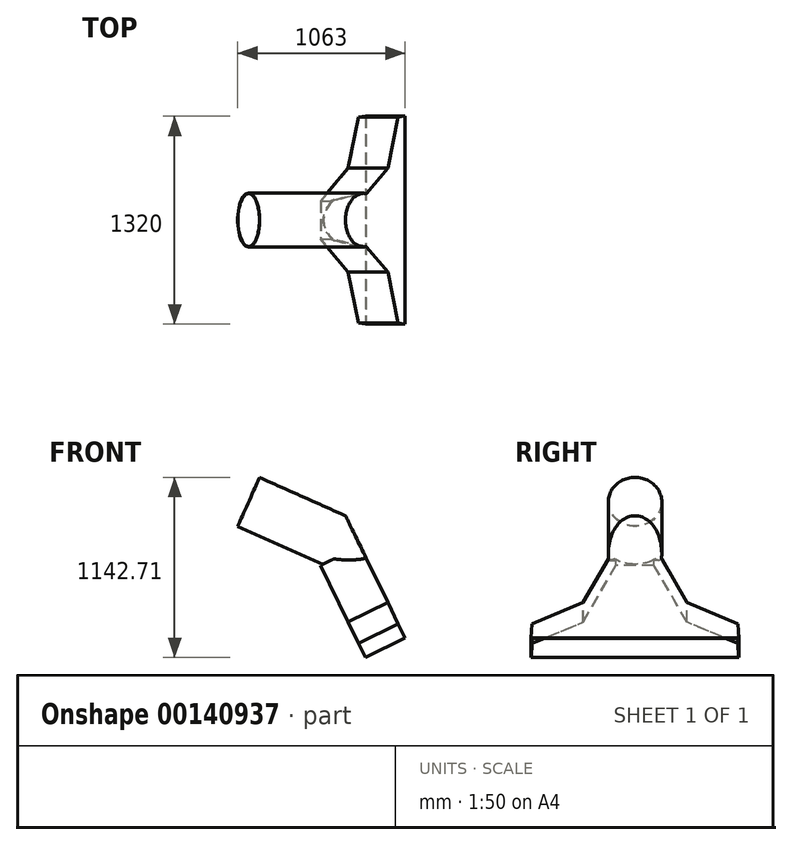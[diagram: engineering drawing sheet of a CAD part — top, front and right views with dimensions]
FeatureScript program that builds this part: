
annotation { "Feature Type Name" : "Feature", "Feature Type Description" : "" }
export const myFeature = defineFeature(function(context is Context, id is Id, definition is map)
    precondition{}
    {
        {
            var Q0;
            Q0=qCreatedBy(makeId("Front.planeOp"),FACE);
            var sketch = newSketch(context, id + "F0", { "sketchPlane" : qUnion([Q0])});
            skLineSegment(sketch, "E0", {"start": v(0, 0) * mm, "end": v(-33.98, 69.66) * mm});
            skSolve(sketch);
        }
        {
            var Q0;
            Q0=qCreatedBy(makeId("Right.planeOp"),FACE);
            var sketch = newSketch(context, id + "F1", { "sketchPlane" : qUnion([Q0])});
            skLineSegment(sketch, "E1", {"start": v(0, 0) * mm, "end": v(61.93, 0) * mm});
            skSolve(sketch);
        }
        {
            var Q0;
            Q0=sQuery(id+"F1.wireOp",EDGE,"E1");
            var Q1;
            Q1=sQuery(id+"F0.wireOp",EDGE,"E0");
            cPlane(context, id + "F2", {"entities" : qUnion([Q0, Q1]), "cplaneType" : CPlaneType.LINE_ANGLE, "offset" : 25 * mm, "angle" : 0 * degree, "width" : 150 * mm, "height" : 150 * mm});
        }
        {
            var Q0;
            Q0=qCreatedBy(id+"F2.planeOp",FACE);
            var sketch = newSketch(context, id + "F3", { "sketchPlane" : qUnion([Q0])});
            skLineSegment(sketch, "E2", {"start": v(0, 0) * mm, "end": v(-660, 0) * mm});
            skLineSegment(sketch, "E3", {"start": v(-660, 0) * mm, "end": v(-654.76, 100) * mm});
            skLineSegment(sketch, "E4", {"start": v(-654.76, 100) * mm, "end": v(-330, 250) * mm});
            skLineSegment(sketch, "E5", {"start": v(-330, 250) * mm, "end": v(-121.77, 650) * mm});
            skLineSegment(sketch, "E6", {"start": v(-121.77, 650) * mm, "end": v(0, 650) * mm});
            skLineSegment(sketch, "E7", {"start": v(0, 0) * mm, "end": v(0, 789.5) * mm, "construction": true});
            skLineSegment(sketch, "E8.MirrorCS", {"start": v(121.77, 650) * mm, "end": v(0, 650) * mm});
            skLineSegment(sketch, "E9.MirrorCS", {"start": v(330, 250) * mm, "end": v(121.77, 650) * mm});
            skLineSegment(sketch, "E10.MirrorCS", {"start": v(654.76, 100) * mm, "end": v(330, 250) * mm});
            skLineSegment(sketch, "E11.MirrorCS", {"start": v(660, 0) * mm, "end": v(654.76, 100) * mm});
            skLineSegment(sketch, "E12.MirrorCS", {"start": v(0, 0) * mm, "end": v(660, 0) * mm});
            skLineSegment(sketch, "E13", {"start": v(-660, 0) * mm, "end": v(-660, 232.34) * mm, "construction": true});
            skPoint(sketch, "E14", {"position": v(0, 600) * mm});
            skSolve(sketch);
        }
        {
            var Q0;
            Q0=makeQuery(id+"F3.imprint","IMPRINT",FACE,{"disambiguationData":[TD([[makeQuery(id+"F3.imprint","IMPRINT",EDGE,{"derivedFrom":sQuery(id+"F3.wireOp",EDGE,"E2")}),-1.0]])]});
            var Q1;
            Q1=qCreatedBy(makeId("Right.planeOp"),FACE);
            extrude(context, id + "F4", {"entities" : qUnion([Q0]), "oppositeDirection" : true, "endBoundEntityFace" : qUnion([Q1]), "depth" : 280 * mm});
        }
        {
            var Q0;
            Q0=qCreatedBy(makeId("Front.planeOp"),FACE);
            var sketch = newSketch(context, id + "F5", { "sketchPlane" : qUnion([Q0])});
            skLineSegment(sketch, "E15", {"start": v(-263.02, 539.28) * mm, "end": v(-993.86, 864.67) * mm});
            skSolve(sketch);
        }
        {
            var Q0;
            Q0=sQuery(id+"F5.wireOp",VERTEX,"E15.end");
            var Q1;
            Q1=sQuery(id+"F5.wireOp",EDGE,"E15");
            cPlane(context, id + "F6", {"entities" : qUnion([Q0, Q1]), "cplaneType" : CPlaneType.LINE_POINT, "offset" : 25 * mm, "width" : 150 * mm, "height" : 150 * mm});
        }
        {
            var Q0;
            Q0=qCreatedBy(id+"F6.planeOp",FACE);
            var sketch = newSketch(context, id + "F7", { "sketchPlane" : qUnion([Q0])});
            skCircle(sketch, "E16", {"center": v(0, 385.67) * mm, "radius": 170 * mm});
            skSolve(sketch);
        }
        {
            var Q0;
            Q0=makeQuery(id+"F7.imprint","IMPRINT",FACE,{"disambiguationData":[TD([[makeQuery(id+"F7.imprint","IMPRINT",EDGE,{"derivedFrom":sQuery(id+"F7.wireOp",EDGE,"E16")}),1.0]])]});
            var Q1;
            Q1=makeQuery(id+"F4.opExtrude","CAP_FACE",FACE,{"disambiguationData":[OSD([sQuery(id+"F3.wireOp",EDGE,"E2"),sQuery(id+"F3.wireOp",EDGE,"E3"),sQuery(id+"F3.wireOp",EDGE,"E4"),sQuery(id+"F3.wireOp",EDGE,"E5"),sQuery(id+"F3.wireOp",EDGE,"E6"),sQuery(id+"F3.wireOp",EDGE,"E8.MirrorCS"),sQuery(id+"F3.wireOp",EDGE,"E9.MirrorCS"),sQuery(id+"F3.wireOp",EDGE,"E10.MirrorCS"),sQuery(id+"F3.wireOp",EDGE,"E11.MirrorCS"),sQuery(id+"F3.wireOp",EDGE,"E12.MirrorCS")])],"isStart":true});
            extrude(context, id + "F8", {"entities" : qUnion([Q0]), "operationType" : NewBodyOperationType.ADD, "endBound" : BoundingType.UP_TO_SURFACE, "oppositeDirection" : true, "endBoundEntityFace" : qUnion([Q1]), "depth" : 25 * mm});
        }
        {
            var Q0;
            Q0=makeQuery(id+"F8.opExtrude","CAP_FACE",FACE,{"disambiguationData":[OSD([sQuery(id+"F7.wireOp",EDGE,"E16")])],"isStart":true});
            var Q1;
            Q1=makeQuery(id+"F4.opExtrude","SWEPT_FACE",FACE,{"disambiguationData":[OSD([sQuery(id+"F3.wireOp",EDGE,"E2"),sQuery(id+"F3.wireOp",EDGE,"E12.MirrorCS")])]});
            shell(context, id + "F9", {"entities" : qUnion([Q0, Q1]), "thickness" : 2 * mm});
        }
        {
            var Q0;
            Q0=makeQuery(id+"F8.boolean.opBoolean","INTERSECT",EDGE,{"derivedFrom":[makeQuery(id+"F4.opExtrude","SWEPT_FACE",FACE,{"disambiguationData":[OSD([sQuery(id+"F3.wireOp",EDGE,"E5")])]}),makeQuery(id+"F8.opExtrude","SWEPT_FACE",FACE,{"disambiguationData":[OSD([sQuery(id+"F7.wireOp",EDGE,"E16")])]})]});
            var Q1;
            Q1=makeQuery(id+"F8.boolean.opBoolean","INTERSECT",EDGE,{"derivedFrom":[makeQuery(id+"F4.opExtrude","SWEPT_FACE",FACE,{"disambiguationData":[OSD([sQuery(id+"F3.wireOp",EDGE,"E9.MirrorCS")])]}),makeQuery(id+"F8.opExtrude","SWEPT_FACE",FACE,{"disambiguationData":[OSD([sQuery(id+"F7.wireOp",EDGE,"E16")])]})]});
            fillet(context, id + "F10", {"entities" : qUnion([Q0, Q1]), "radius" : 12 * mm, "tangentPropagation" : true, "allowEdgeOverflow" : false});
        }
    });
